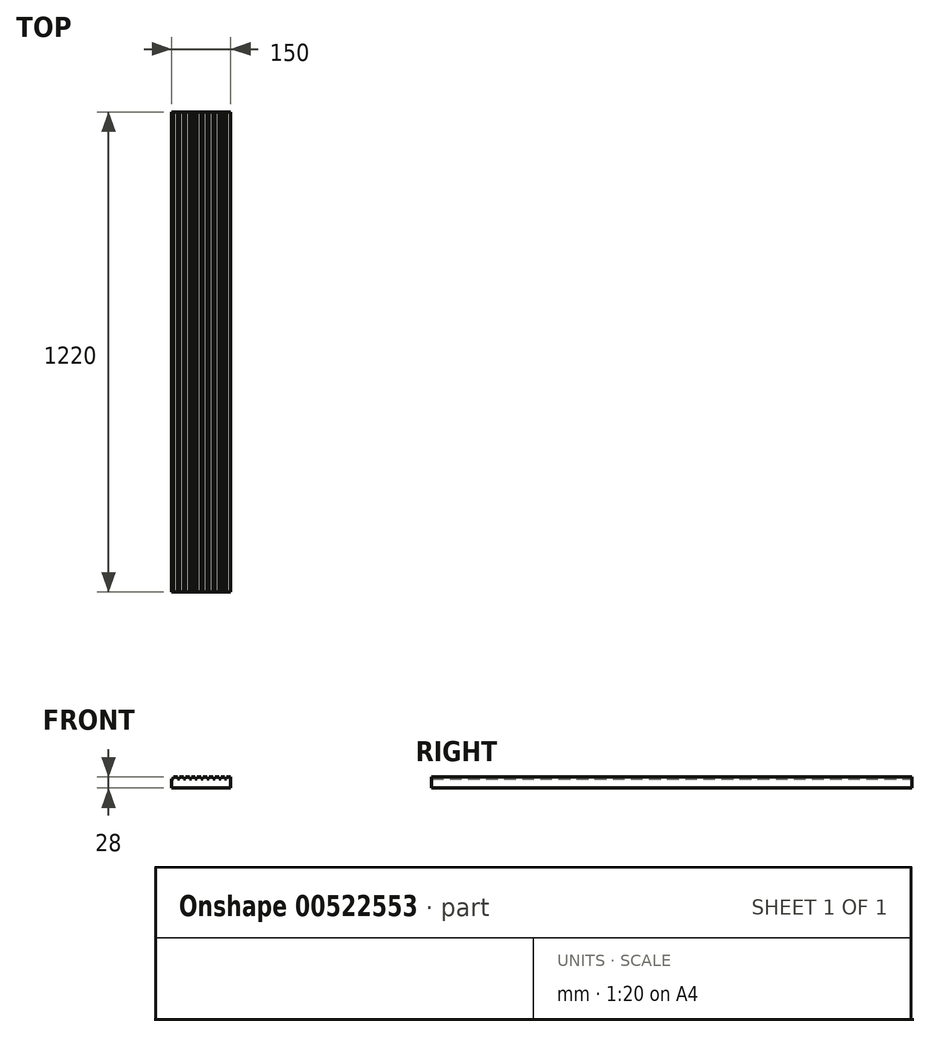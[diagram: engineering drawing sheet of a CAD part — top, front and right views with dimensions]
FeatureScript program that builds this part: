
annotation { "Feature Type Name" : "Feature", "Feature Type Description" : "" }
export const myFeature = defineFeature(function(context is Context, id is Id, definition is map)
    precondition{}
    {
        {
            var Q0;
            Q0=qCreatedBy(makeId("Front.planeOp"),FACE);
            var sketch = newSketch(context, id + "F0", { "sketchPlane" : qUnion([Q0])});
            skLineSegment(sketch, "E0", {"start": v(0, 0) * mm, "end": v(0, 28) * mm});
            skLineSegment(sketch, "E1", {"start": v(0, 28) * mm, "end": v(-10, 28) * mm});
            skLineSegment(sketch, "E2", {"start": v(-10, 28) * mm, "end": v(-10, 23) * mm});
            skLineSegment(sketch, "E3", {"start": v(-10, 23) * mm, "end": v(-15, 23) * mm});
            skLineSegment(sketch, "E4", {"start": v(-15, 23) * mm, "end": v(-15, 28) * mm});
            skLineSegment(sketch, "E5", {"start": v(-15, 28) * mm, "end": v(-25, 28) * mm});
            skLineSegment(sketch, "E6", {"start": v(-25, 28) * mm, "end": v(-25, 23) * mm});
            skLineSegment(sketch, "E7", {"start": v(-25, 23) * mm, "end": v(-30, 23) * mm});
            skLineSegment(sketch, "E8", {"start": v(-30, 23) * mm, "end": v(-30, 28) * mm});
            skLineSegment(sketch, "E9", {"start": v(-30, 28) * mm, "end": v(-40, 28) * mm});
            skLineSegment(sketch, "E10", {"start": v(-40, 28) * mm, "end": v(-40, 23) * mm});
            skLineSegment(sketch, "E11", {"start": v(-40, 23) * mm, "end": v(-45, 23) * mm});
            skLineSegment(sketch, "E12", {"start": v(-45, 23) * mm, "end": v(-45, 28) * mm});
            skLineSegment(sketch, "E13", {"start": v(-45, 28) * mm, "end": v(-55, 28) * mm});
            skLineSegment(sketch, "E14", {"start": v(-55, 28) * mm, "end": v(-55, 23) * mm});
            skLineSegment(sketch, "E15", {"start": v(-55, 23) * mm, "end": v(-60, 23) * mm});
            skLineSegment(sketch, "E16", {"start": v(-60, 23) * mm, "end": v(-60, 28) * mm});
            skLineSegment(sketch, "E17", {"start": v(-60, 28) * mm, "end": v(-70, 28) * mm});
            skLineSegment(sketch, "E18", {"start": v(-70, 28) * mm, "end": v(-70, 23) * mm});
            skLineSegment(sketch, "E19", {"start": v(-70, 23) * mm, "end": v(-75, 23) * mm});
            skLineSegment(sketch, "E20", {"start": v(-75, 23) * mm, "end": v(-75, 28) * mm});
            skLineSegment(sketch, "E21", {"start": v(-75, 28) * mm, "end": v(-85, 28) * mm});
            skLineSegment(sketch, "E22", {"start": v(-85, 28) * mm, "end": v(-85, 23) * mm});
            skLineSegment(sketch, "E23", {"start": v(-85, 23) * mm, "end": v(-90, 23) * mm});
            skLineSegment(sketch, "E24", {"start": v(-90, 23) * mm, "end": v(-90, 28) * mm});
            skLineSegment(sketch, "E25", {"start": v(-90, 28) * mm, "end": v(-100, 28) * mm});
            skLineSegment(sketch, "E26", {"start": v(-100, 28) * mm, "end": v(-100, 23) * mm});
            skLineSegment(sketch, "E27", {"start": v(-100, 23) * mm, "end": v(-105, 23) * mm});
            skLineSegment(sketch, "E28", {"start": v(-105, 23) * mm, "end": v(-105, 28) * mm});
            skLineSegment(sketch, "E29", {"start": v(-105, 28) * mm, "end": v(-115, 28) * mm});
            skLineSegment(sketch, "E30", {"start": v(-115, 28) * mm, "end": v(-115, 23) * mm});
            skLineSegment(sketch, "E31", {"start": v(-115, 23) * mm, "end": v(-120, 23) * mm});
            skLineSegment(sketch, "E32", {"start": v(-120, 23) * mm, "end": v(-120, 28) * mm});
            skLineSegment(sketch, "E33", {"start": v(-120, 28) * mm, "end": v(-130, 28) * mm});
            skLineSegment(sketch, "E34", {"start": v(-130, 28) * mm, "end": v(-130, 23) * mm});
            skLineSegment(sketch, "E35", {"start": v(-130, 23) * mm, "end": v(-135, 23) * mm});
            skLineSegment(sketch, "E36", {"start": v(-135, 23) * mm, "end": v(-135, 28) * mm});
            skLineSegment(sketch, "E37", {"start": v(-135, 28) * mm, "end": v(-145, 28) * mm});
            skLineSegment(sketch, "E38", {"start": v(-145, 28) * mm, "end": v(-145, 23) * mm});
            skLineSegment(sketch, "E39", {"start": v(-145, 23) * mm, "end": v(-150, 23) * mm});
            skLineSegment(sketch, "E40", {"start": v(-150, 23) * mm, "end": v(-150, 0) * mm});
            skLineSegment(sketch, "E41", {"start": v(-150, 0) * mm, "end": v(0, 0) * mm});
            skSolve(sketch);
        }
        {
            var Q0;
            Q0 = qSketchRegion(id + "F0", true);
            extrude(context, id + "F1", {"entities" : qUnion([Q0]), "depth" : 1220 * mm, "offsetDistance" : 25 * mm});
        }
    });
